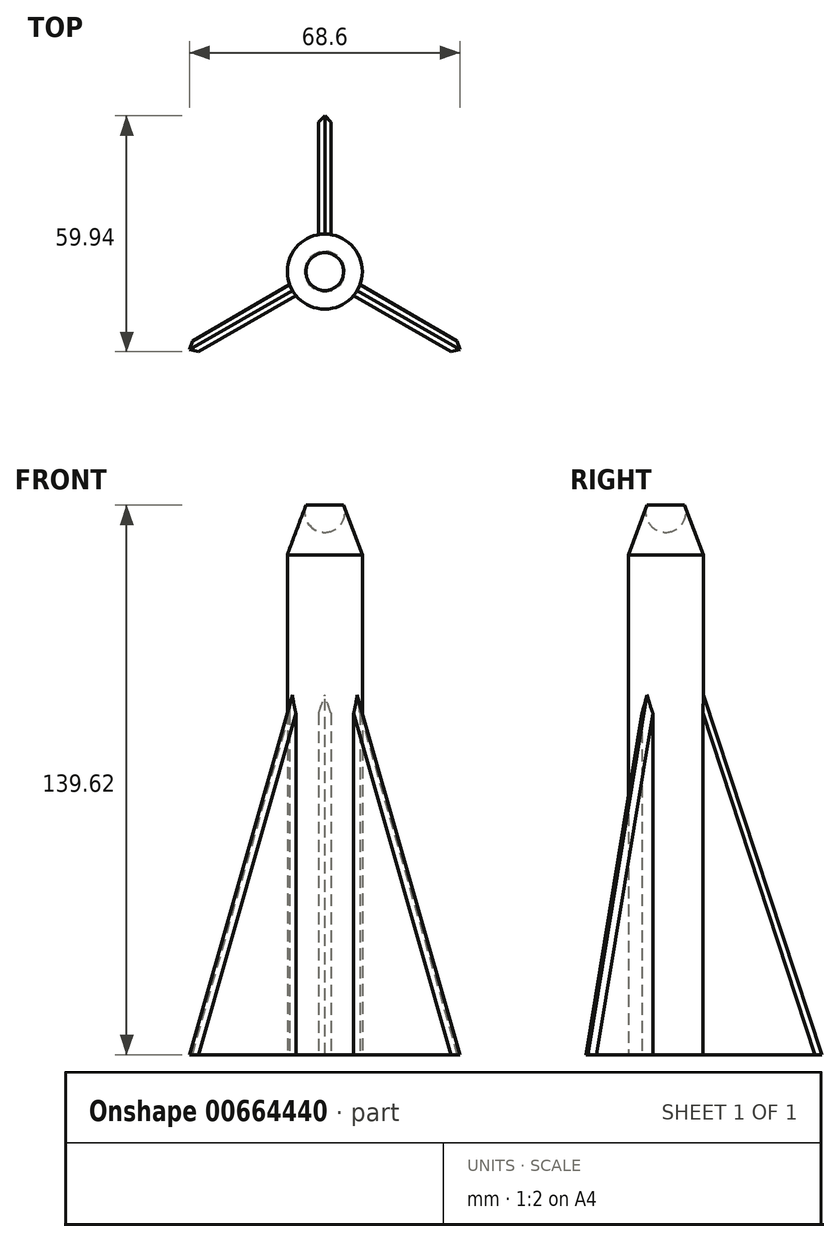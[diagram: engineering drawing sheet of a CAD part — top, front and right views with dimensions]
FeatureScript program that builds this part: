
annotation { "Feature Type Name" : "Feature", "Feature Type Description" : "" }
export const myFeature = defineFeature(function(context is Context, id is Id, definition is map)
    precondition{}
    {
        {
            var Q0;
            Q0=qCreatedBy(makeId("Top.planeOp"),FACE);
            var sketch = newSketch(context, id + "F0", { "sketchPlane" : qUnion([Q0])});
            skCircle(sketch, "E0", {"center": v(0, 0) * mm, "radius": 9.52 * mm});
            skSolve(sketch);
        }
        {
            var Q0;
            Q0 = qSketchRegion(id + "F0", true);
            extrude(context, id + "F1", {"entities" : qUnion([Q0]), "depth" : 127 * mm, "offsetDistance" : 25.4 * mm});
        }
        {
            var Q0;
            Q0=qCreatedBy(makeId("Front.planeOp"),FACE);
            var sketch = newSketch(context, id + "F2", { "sketchPlane" : qUnion([Q0])});
            skLineSegment(sketch, "E1.0.0", {"start": v(-9.52, 127) * mm, "end": v(9.52, 127) * mm});
            skLineSegment(sketch, "E2", {"start": v(-9.53, 127) * mm, "end": v(0, 152.4) * mm});
            skLineSegment(sketch, "E3", {"start": v(0, 127) * mm, "end": v(0, 152.4) * mm});
            skSolve(sketch);
        }
        {
            var Q0;
            {var subQ0=sQuery(id+"F2.wireOp",EDGE,"E2");Q0=makeQuery(id+"F2.imprint","IMPRINT",FACE,{"disambiguationData":[TD([[makeQuery(id+"F2.imprint","IMPRINT",EDGE,{"derivedFrom":subQ0}),-1.0]])]});}
            var Q1;
            Q1=sQuery(id+"F2.wireOp",EDGE,"E3");
            revolve(context, id + "F3", {"operationType" : NewBodyOperationType.ADD, "entities" : qUnion([Q0]), "axis" : qUnion([Q1]), "revolveType" : RevolveType.FULL});
        }
        {
            var Q0;
            Q0=qCreatedBy(makeId("Right.planeOp"),FACE);
            var sketch = newSketch(context, id + "F4", { "sketchPlane" : qUnion([Q0])});
            skLineSegment(sketch, "E4", {"start": v(-9.52, 0) * mm, "end": v(-9.52, 127) * mm});
            skLineSegment(sketch, "E5", {"start": v(9.52, 193.02) * mm, "end": v(9.52, 0) * mm});
            skLineSegment(sketch, "E6", {"start": v(9.53, 0) * mm, "end": v(41.27, 0) * mm});
            skLineSegment(sketch, "E7", {"start": v(41.27, 0) * mm, "end": v(9.53, 96.51) * mm});
            skLineSegment(sketch, "E8", {"start": v(9.52, 96.51) * mm, "end": v(3.64, 96.51) * mm});
            skLineSegment(sketch, "E9", {"start": v(3.64, 96.51) * mm, "end": v(3.64, 0) * mm});
            skLineSegment(sketch, "E10", {"start": v(3.64, 0) * mm, "end": v(9.52, 0) * mm});
            skSolve(sketch);
        }
        {
            var Q0;
            Q0 = qSketchRegion(id + "F4", true);
            extrude(context, id + "F5", {"entities" : qUnion([Q0]), "operationType" : NewBodyOperationType.ADD, "endBound" : BoundingType.SYMMETRIC, "depth" : 3.17 * mm, "offsetDistance" : 25.4 * mm});
        }
        {
            var Q0;
            Q0=makeQuery(id+"F5.opExtrude","CAP_EDGE",EDGE,{"disambiguationData":[OSD([sQuery(id+"F4.wireOp",EDGE,"E7")])],"isStart":false});
            var Q1;
            Q1=makeQuery(id+"F5.opExtrude","CAP_EDGE",EDGE,{"disambiguationData":[OSD([sQuery(id+"F4.wireOp",EDGE,"E7")])],"isStart":true});
            chamfer(context, id + "F6", {"entities" : qUnion([Q0, Q1]), "width" : 3.17 * mm, "tangentPropagation" : true});
        }
        {
            var Q0;
            Q0=makeQuery(id+"F1.opExtrude","SWEPT_BODY",BODY,{"disambiguationData":[OSD([sQuery(id+"F0.wireOp",EDGE,"E0")])]});
            var Q1;
            Q1=makeQuery(id+"F1.opExtrude","SWEPT_FACE",FACE,{"disambiguationData":[OSD([sQuery(id+"F0.wireOp",EDGE,"E0")])]});
            circularPattern(context, id + "F7", {"operationType" : NewBodyOperationType.ADD, "entities" : qUnion([Q0]), "axis" : qUnion([Q1]), "angle" : 360 * degree, "instanceCount" : 3, "equalSpace" : true});
        }
        {
            var Q0;
            Q0=qCreatedBy(makeId("Front.planeOp"),FACE);
            var sketch = newSketch(context, id + "F8", { "sketchPlane" : qUnion([Q0])});
            skLineSegment(sketch, "E11", {"start": v(-9.52, 127) * mm, "end": v(0, 152.4) * mm});
            skLineSegment(sketch, "E12", {"start": v(0, 152.4) * mm, "end": v(9.52, 127) * mm});
            skCircle(sketch, "E13", {"center": v(0, 137.83) * mm, "radius": 5.12 * mm, "construction": true});
            skPoint(sketch, "E14", {"position": v(4.8, 139.62) * mm});
            skLineSegment(sketch, "E15", {"start": v(0, 152.4) * mm, "end": v(0, 132.71) * mm});
            skArc(sketch, "E16", {"start": v(0, 132.71) * mm, "mid": v(4.2, 134.91) * mm, "end": v(4.8, 139.62) * mm});
            skSolve(sketch);
        }
        {
            var Q0;
            Q0 = qSketchRegion(id + "F8", true);
            var Q1;
            Q1=sQuery(id+"F8.wireOp",EDGE,"E15");
            revolve(context, id + "F9", {"operationType" : NewBodyOperationType.REMOVE, "surfaceOperationType" : NewSurfaceOperationType.NEW, "entities" : qUnion([Q0]), "axis" : qUnion([Q1]), "revolveType" : RevolveType.FULL, "oppositeDirection" : true});
        }
    });
